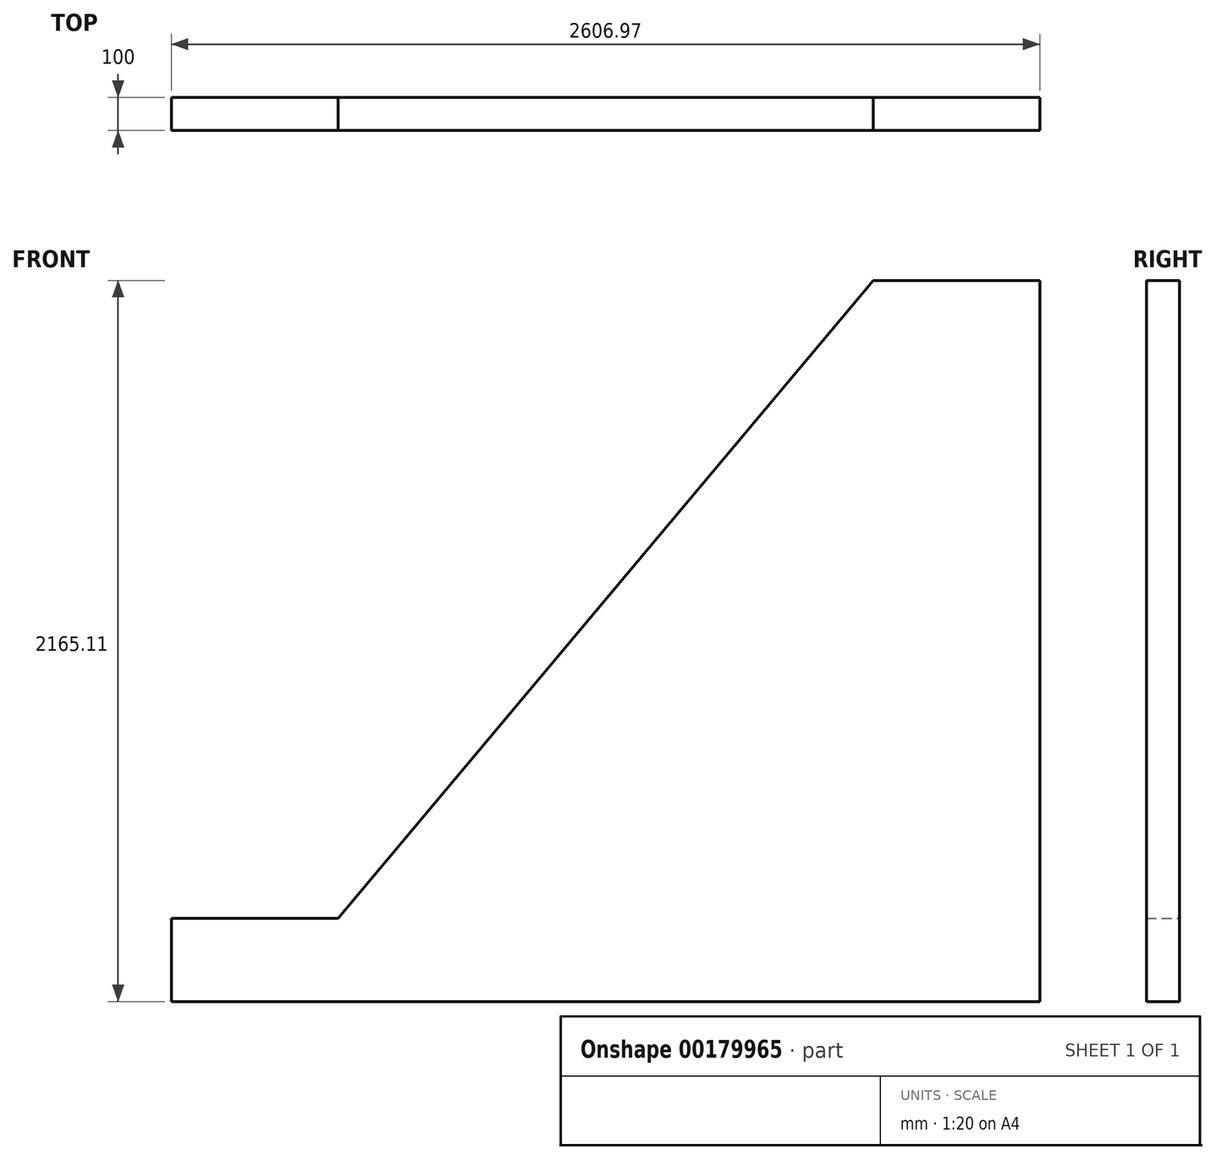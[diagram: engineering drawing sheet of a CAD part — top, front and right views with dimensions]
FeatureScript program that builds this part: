
annotation { "Feature Type Name" : "Feature", "Feature Type Description" : "" }
export const myFeature = defineFeature(function(context is Context, id is Id, definition is map)
    precondition{}
    {
        {
            var Q0;
            Q0=qCreatedBy(makeId("Front.planeOp"),FACE);
            var sketch = newSketch(context, id + "F0", { "sketchPlane" : qUnion([Q0])});
            skLineSegment(sketch, "E0", {"start": v(0, 0) * mm, "end": v(500, 0) * mm});
            skLineSegment(sketch, "E1", {"start": v(500, 0) * mm, "end": v(2106.97, 1915.11) * mm});
            skLineSegment(sketch, "E2", {"start": v(2106.97, 1915.11) * mm, "end": v(2606.97, 1915.11) * mm});
            skLineSegment(sketch, "E3", {"start": v(0, 0) * mm, "end": v(0, -250) * mm});
            skLineSegment(sketch, "E4", {"start": v(0, -250) * mm, "end": v(2606.97, -250) * mm});
            skLineSegment(sketch, "E5", {"start": v(2606.97, -250) * mm, "end": v(2606.97, 1915.11) * mm});
            skSolve(sketch);
        }
        {
            var Q0;
            Q0=qSketchRegion(id+"F0",true);
            extrude(context, id + "F1", {"entities" : qUnion([Q0]), "depth" : 100 * mm});
        }
    });
